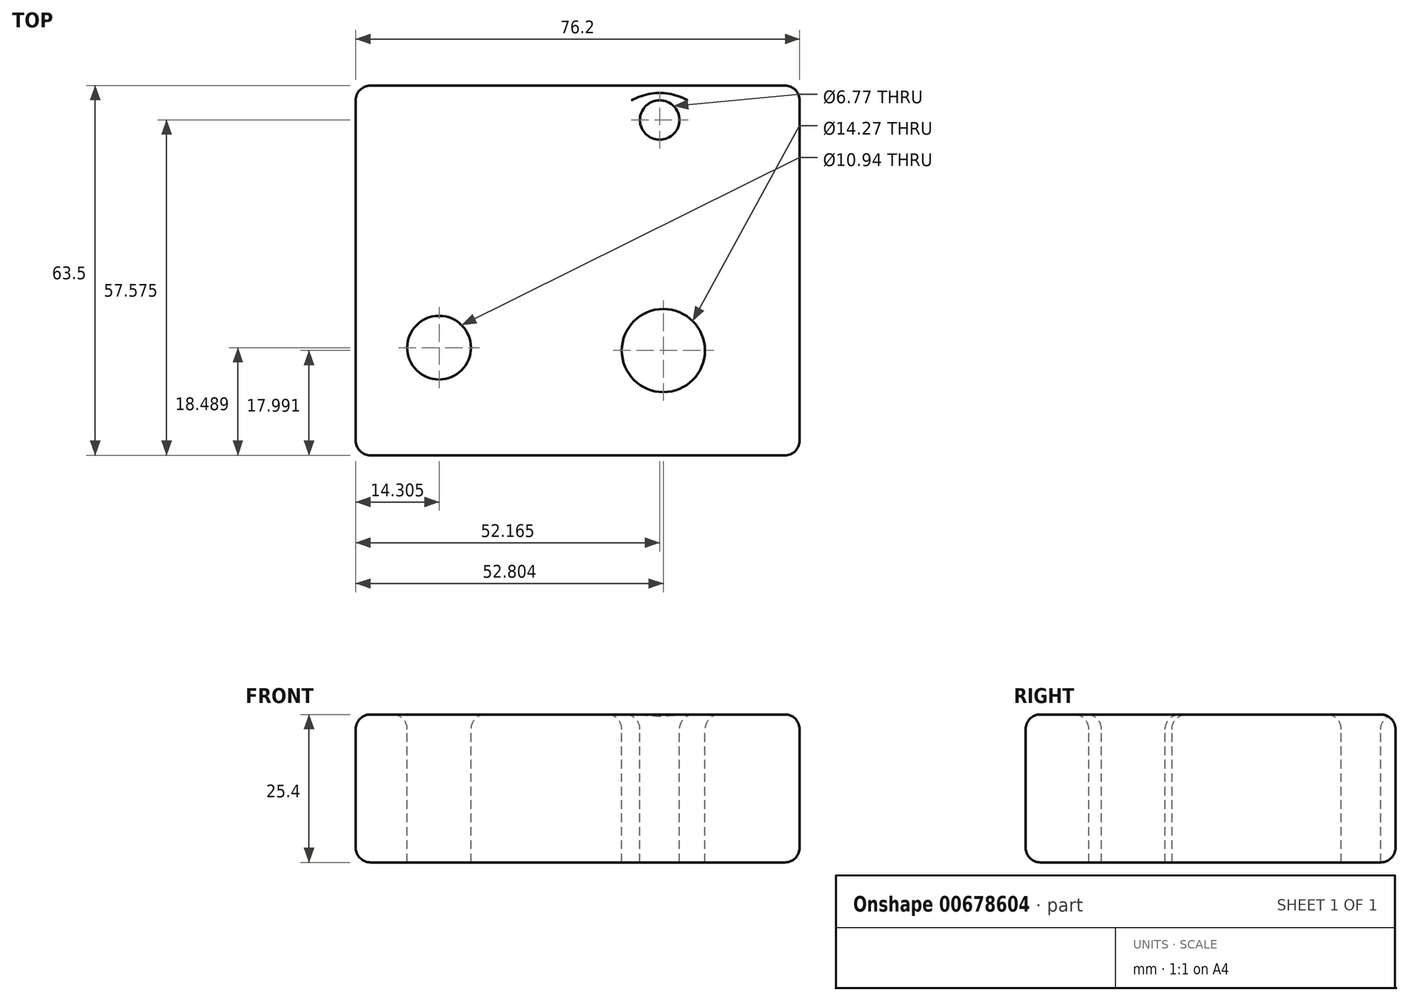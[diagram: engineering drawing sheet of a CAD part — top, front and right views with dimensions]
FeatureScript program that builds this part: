
annotation { "Feature Type Name" : "Feature", "Feature Type Description" : "" }
export const myFeature = defineFeature(function(context is Context, id is Id, definition is map)
    precondition{}
    {
        {
            var Q0;
            Q0=qCreatedBy(makeId("Top.planeOp"),FACE);
            var sketch = newSketch(context, id + "F0", { "sketchPlane" : qUnion([Q0])});
            skLineSegment(sketch, "E0.bottom", {"start": v(-38.1, 31.75) * mm, "end": v(38.1, 31.75) * mm});
            skLineSegment(sketch, "E0.top", {"start": v(-38.1, -31.75) * mm, "end": v(38.1, -31.75) * mm});
            skLineSegment(sketch, "E0.left", {"start": v(-38.1, 31.75) * mm, "end": v(-38.1, -31.75) * mm});
            skLineSegment(sketch, "E0.right", {"start": v(38.1, 31.75) * mm, "end": v(38.1, -31.75) * mm});
            skPoint(sketch, "E0.middle", {"position": v(0, 0) * mm});
            skSolve(sketch);
        }
        {
            var Q0;
            Q0 = qSketchRegion(id + "F0", true);
            extrude(context, id + "F1", {"entities" : qUnion([Q0]), "depth" : 25.4 * mm, "offsetDistance" : 25.4 * mm});
        }
        {
            var Q0;
            Q0=makeQuery(id+"F1.opExtrude","CAP_FACE",FACE,{"disambiguationData":[OSD([sQuery(id+"F0.wireOp",EDGE,"E0.bottom"),sQuery(id+"F0.wireOp",EDGE,"E0.top"),sQuery(id+"F0.wireOp",EDGE,"E0.left"),sQuery(id+"F0.wireOp",EDGE,"E0.right")])],"isStart":false});
            var sketch = newSketch(context, id + "F2", { "sketchPlane" : qUnion([Q0])});
            skCircle(sketch, "E1", {"center": v(-23.8, -13.26) * mm, "radius": 5.47 * mm});
            skCircle(sketch, "E2", {"center": v(14.7, -13.76) * mm, "radius": 7.14 * mm});
            skCircle(sketch, "E3", {"center": v(14.07, 25.83) * mm, "radius": 3.39 * mm});
            skSolve(sketch);
        }
        {
            var Q0;
            Q0 = qSketchRegion(id + "F2", true);
            extrude(context, id + "F3", {"entities" : qUnion([Q0]), "operationType" : NewBodyOperationType.REMOVE, "endBound" : BoundingType.THROUGH_ALL, "oppositeDirection" : true, "depth" : 25.4 * mm, "offsetDistance" : 25.4 * mm});
        }
        {
            var Q0;
            Q0=makeQuery(id+"F1.opExtrude","CAP_FACE",FACE,{"disambiguationData":[OSD([sQuery(id+"F0.wireOp",EDGE,"E0.bottom"),sQuery(id+"F0.wireOp",EDGE,"E0.top"),sQuery(id+"F0.wireOp",EDGE,"E0.left"),sQuery(id+"F0.wireOp",EDGE,"E0.right")])],"isStart":false});
            fillet(context, id + "F4", {"entities" : qUnion([Q0]), "radius" : 2.54 * mm, "tangentPropagation" : true, "allowEdgeOverflow" : false});
        }
        {
            var Q0;
            Q0=makeQuery(id+"F1.opExtrude","SWEPT_FACE",FACE,{"disambiguationData":[OSD([sQuery(id+"F0.wireOp",EDGE,"E0.left")])]});
            var Q1;
            Q1=makeQuery(id+"F1.opExtrude","SWEPT_FACE",FACE,{"disambiguationData":[OSD([sQuery(id+"F0.wireOp",EDGE,"E0.top")])]});
            var Q2;
            Q2=makeQuery(id+"F1.opExtrude","SWEPT_FACE",FACE,{"disambiguationData":[OSD([sQuery(id+"F0.wireOp",EDGE,"E0.bottom")])]});
            var Q3;
            Q3=makeQuery(id+"F1.opExtrude","SWEPT_FACE",FACE,{"disambiguationData":[OSD([sQuery(id+"F0.wireOp",EDGE,"E0.right")])]});
            fillet(context, id + "F5", {"entities" : qUnion([Q0, Q1, Q2, Q3]), "radius" : 2.54 * mm, "tangentPropagation" : true, "allowEdgeOverflow" : false});
        }
    });
